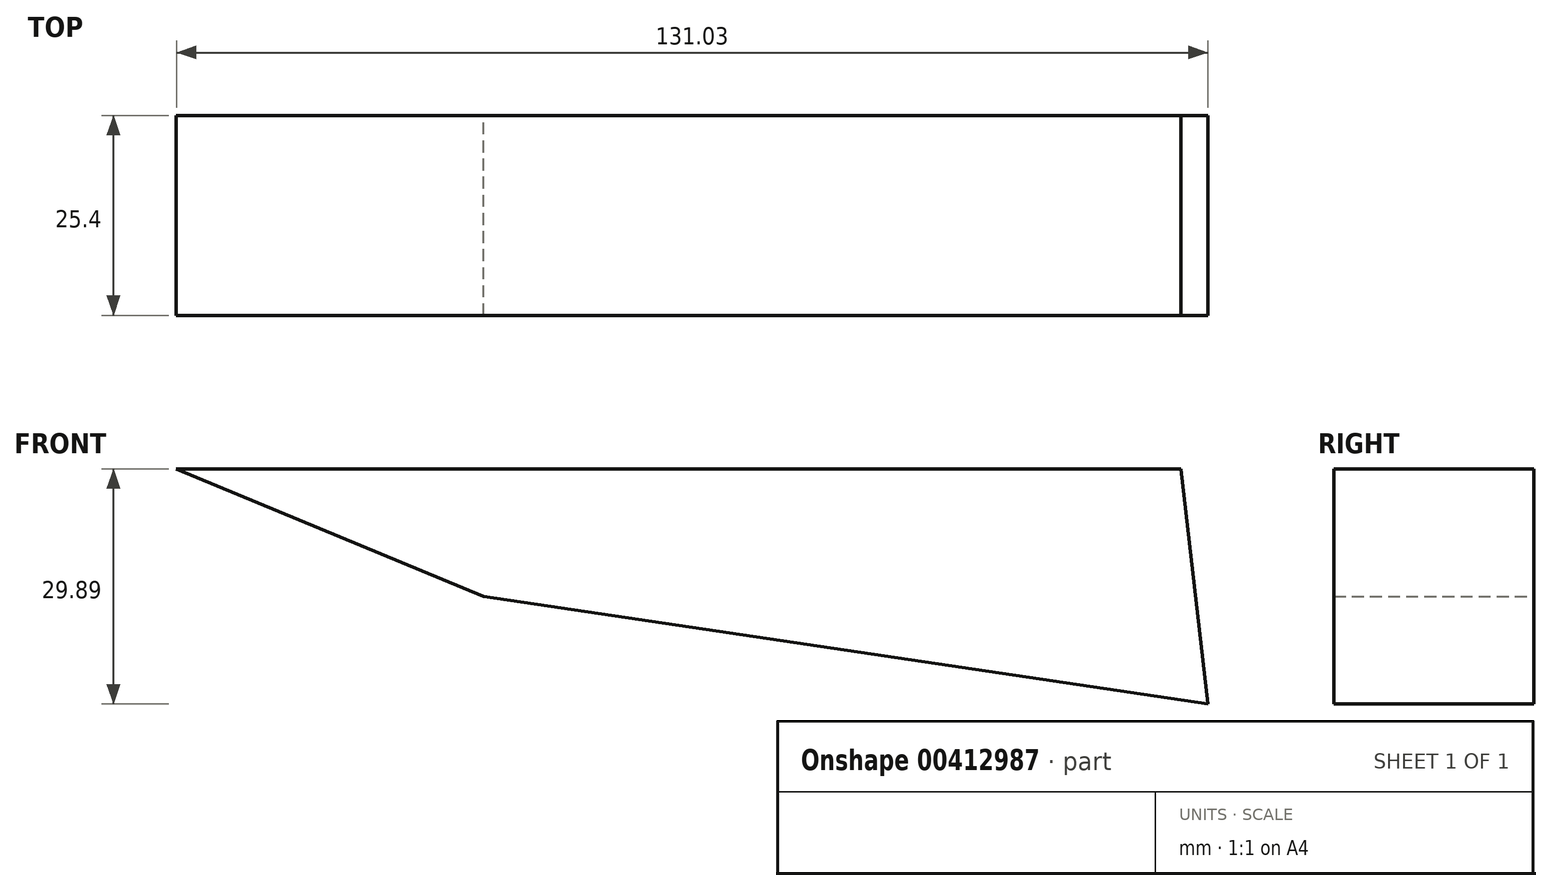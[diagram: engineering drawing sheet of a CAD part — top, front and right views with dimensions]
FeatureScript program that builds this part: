
annotation { "Feature Type Name" : "Feature", "Feature Type Description" : "" }
export const myFeature = defineFeature(function(context is Context, id is Id, definition is map)
    precondition{}
    {
        {
            var Q0;
            Q0=qCreatedBy(makeId("Front.planeOp"),FACE);
            var sketch = newSketch(context, id + "F0", { "sketchPlane" : qUnion([Q0])});
            skLineSegment(sketch, "E0", {"start": v(0, 0) * mm, "end": v(60.99, 0) * mm});
            skLineSegment(sketch, "E1", {"start": v(60.99, 0) * mm, "end": v(64.41, -29.9) * mm});
            skLineSegment(sketch, "E2", {"start": v(64.41, -29.9) * mm, "end": v(-27.58, -16.2) * mm});
            skLineSegment(sketch, "E3", {"start": v(-27.58, -16.2) * mm, "end": v(-66.62, 0) * mm});
            skLineSegment(sketch, "E4", {"start": v(-66.62, 0) * mm, "end": v(0, 0) * mm});
            skSolve(sketch);
        }
        {
            var Q0;
            Q0=makeQuery(id+"F0.imprint","IMPRINT",FACE,{"disambiguationData":[TD([[makeQuery(id+"F0.imprint","IMPRINT",EDGE,{"derivedFrom":sQuery(id+"F0.wireOp",EDGE,"E0")}),-1.0]])]});
            extrude(context, id + "F1", {"entities" : qUnion([Q0]), "depth" : 25.4 * mm});
        }
    });
